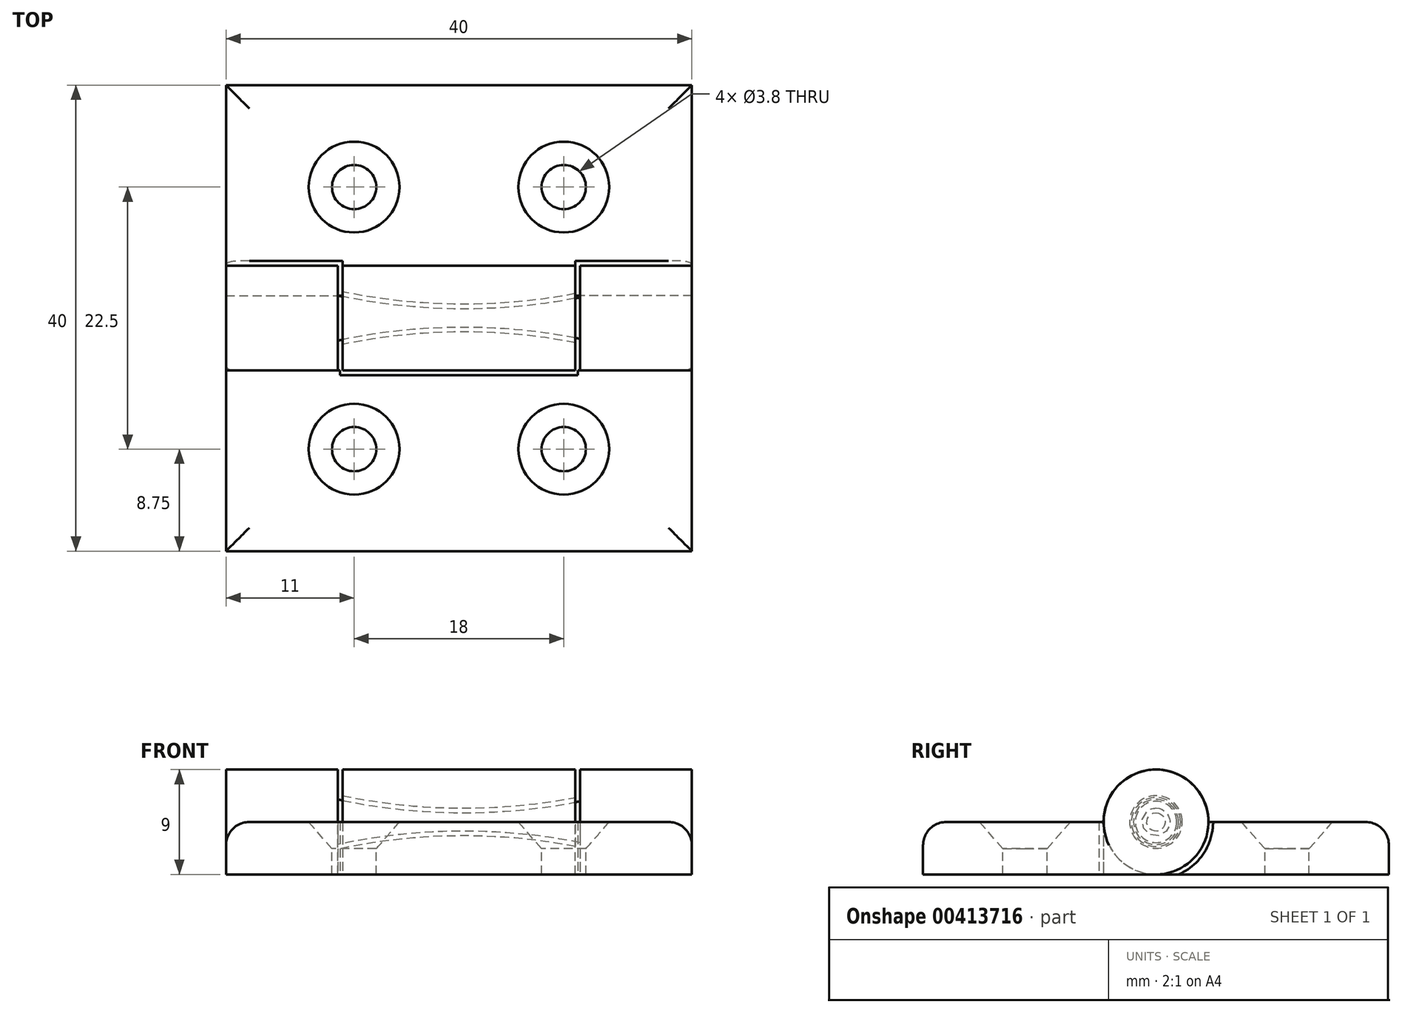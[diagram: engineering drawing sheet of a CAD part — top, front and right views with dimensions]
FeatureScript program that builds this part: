
annotation { "Feature Type Name" : "Feature", "Feature Type Description" : "" }
export const myFeature = defineFeature(function(context is Context, id is Id, definition is map)
    precondition{}
    {
        {
            var Q0;
            Q0=qCreatedBy(makeId("Front.planeOp"),FACE);
            var sketch = newSketch(context, id + "F0", { "sketchPlane" : qUnion([Q0])});
            skLineSegment(sketch, "E0", {"start": v(-18.48, 0) * mm, "end": v(18.23, 0) * mm, "construction": true});
            skLineSegment(sketch, "E1", {"start": v(-10, 18.4) * mm, "end": v(-10, -18.31) * mm, "construction": true});
            skLineSegment(sketch, "E2", {"start": v(10, 18.4) * mm, "end": v(10, -18.31) * mm, "construction": true});
            skLineSegment(sketch, "E3.0", {"start": v(-18.48, 2) * mm, "end": v(18.23, 2) * mm, "construction": true});
            skLineSegment(sketch, "E4.0", {"start": v(-18.48, 1) * mm, "end": v(18.48, 1) * mm, "construction": true});
            skPoint(sketch, "E5", {"position": v(0, 1) * mm});
            skPoint(sketch, "E6", {"position": v(10, 2) * mm});
            skPoint(sketch, "E7", {"position": v(-10, 2) * mm});
            skArc(sketch, "E8", {"start": v(-10, 2) * mm, "mid": v(0, 1) * mm, "end": v(10, 2) * mm});
            skLineSegment(sketch, "E9", {"start": v(-10, 2) * mm, "end": v(-10, 0) * mm});
            skLineSegment(sketch, "E10", {"start": v(-10, 0) * mm, "end": v(10, 0) * mm});
            skLineSegment(sketch, "E11", {"start": v(10, 0) * mm, "end": v(10, 2) * mm});
            skSolve(sketch);
        }
        {
            var Q0;
            Q0=qCreatedBy(makeId("Front.planeOp"),FACE);
            var sketch = newSketch(context, id + "F1", { "sketchPlane" : qUnion([Q0])});
            skLineSegment(sketch, "E12.0", {"start": v(-10, 0) * mm, "end": v(10, 0) * mm});
            skLineSegment(sketch, "E13.0", {"start": v(-10, 1.85) * mm, "end": v(-10, 0) * mm});
            skLineSegment(sketch, "E14.0", {"start": v(10, 0) * mm, "end": v(10, 1.7) * mm});
            skLineSegment(sketch, "E15.0", {"start": v(10.4, 0) * mm, "end": v(10.4, 2.18) * mm});
            skArc(sketch, "E15.1", {"start": v(-10.4, 2.34) * mm, "mid": v(0, 1.2) * mm, "end": v(10.4, 2.18) * mm});
            skLineSegment(sketch, "E15.2", {"start": v(-10.4, 2.34) * mm, "end": v(-10.4, 0) * mm});
            skLineSegment(sketch, "E16", {"start": v(-10.4, 0) * mm, "end": v(-10, 0) * mm});
            skLineSegment(sketch, "E17", {"start": v(-10.4, 2.34) * mm, "end": v(-10.4, 4.5) * mm});
            skLineSegment(sketch, "E18", {"start": v(-10.4, 4.5) * mm, "end": v(10.4, 4.5) * mm});
            skLineSegment(sketch, "E19", {"start": v(10.4, 4.5) * mm, "end": v(10.4, 2.18) * mm});
            skLineSegment(sketch, "E20", {"start": v(-10, 2.26) * mm, "end": v(-10, 4.5) * mm});
            skLineSegment(sketch, "E21", {"start": v(10, 2.1) * mm, "end": v(10, 4.5) * mm});
            skArc(sketch, "E22.0", {"start": v(-10.4, 1.93) * mm, "mid": v(0, 0.8) * mm, "end": v(10.4, 1.77) * mm});
            skLineSegment(sketch, "E23", {"start": v(-10, 2.26) * mm, "end": v(-10, 1.85) * mm});
            skLineSegment(sketch, "E24", {"start": v(10, 2.1) * mm, "end": v(10, 1.7) * mm});
            skLineSegment(sketch, "E25", {"start": v(10.4, 0) * mm, "end": v(10, 0) * mm});
            skSolve(sketch);
        }
        {
            var Q0;
            Q0=makeQuery(id+"F1.imprint","IMPRINT",FACE,{"disambiguationData":[TD([[makeQuery(id+"F1.imprint","IMPRINT",EDGE,{"derivedFrom":sQuery(id+"F1.wireOp",EDGE,"E12.0")}),1.0]])]});
            var Q1;
            {var subQ0=sQuery(id+"F1.wireOp",EDGE,"E13.0");Q1=makeQuery(id+"F1.imprint","IMPRINT",FACE,{"disambiguationData":[TD([[makeQuery(id+"F1.imprint","IMPRINT",EDGE,{"derivedFrom":subQ0}),-1.0]])]});}
            var Q2;
            {var subQ0=sQuery(id+"F1.wireOp",EDGE,"E14.0");Q2=makeQuery(id+"F1.imprint","IMPRINT",FACE,{"disambiguationData":[TD([[makeQuery(id+"F1.imprint","IMPRINT",EDGE,{"derivedFrom":subQ0}),-1.0]])]});}
            var Q3;
            Q3=sQuery(id+"F1.wireOp",EDGE,"E12.0");
            revolve(context, id + "F2", {"entities" : qUnion([Q0, Q1, Q2]), "axis" : qUnion([Q3]), "revolveType" : RevolveType.FULL});
        }
        {
            var Q0;
            {var subQ0=sQuery(id+"F1.wireOp",EDGE,"E20");Q0=makeQuery(id+"F1.imprint","IMPRINT",FACE,{"disambiguationData":[TD([[makeQuery(id+"F1.imprint","IMPRINT",EDGE,{"derivedFrom":subQ0}),-1.0]])]});}
            var Q1;
            Q1=sQuery(id+"F1.wireOp",EDGE,"E12.0");
            revolve(context, id + "F3", {"entities" : qUnion([Q0]), "axis" : qUnion([Q1]), "revolveType" : RevolveType.FULL});
        }
        {
            var Q0;
            Q0=qCreatedBy(makeId("Right.planeOp"),FACE);
            var sketch = newSketch(context, id + "F4", { "sketchPlane" : qUnion([Q0])});
            skPoint(sketch, "E26", {"position": v(4.5, 0) * mm});
            skLineSegment(sketch, "E27.0", {"start": v(-20, 18.4) * mm, "end": v(-20, -18.31) * mm, "construction": true});
            skLineSegment(sketch, "E28", {"start": v(-23.98, 0) * mm, "end": v(20, 0) * mm, "construction": true});
            skLineSegment(sketch, "E29.0", {"start": v(-23.98, -4.5) * mm, "end": v(20, -4.5) * mm, "construction": true});
            skPoint(sketch, "E30", {"position": v(-20, 0) * mm});
            skPoint(sketch, "E31", {"position": v(-20, -4.5) * mm});
            skPoint(sketch, "E32", {"position": v(4.5, -4.5) * mm});
            skLineSegment(sketch, "E33", {"start": v(-20, 0) * mm, "end": v(-20, -4.5) * mm});
            skLineSegment(sketch, "E34", {"start": v(4.5, -4.5) * mm, "end": v(4.5, 0) * mm});
            skLineSegment(sketch, "E35", {"start": v(-20, 0) * mm, "end": v(4.5, 0) * mm});
            skLineSegment(sketch, "E36", {"start": v(4.5, -4.5) * mm, "end": v(-20, -4.5) * mm});
            skLineSegment(sketch, "E37.0", {"start": v(20, 18.4) * mm, "end": v(20, -18.31) * mm, "construction": true});
            skPoint(sketch, "E38", {"position": v(-4.5, 0) * mm});
            skPoint(sketch, "E39", {"position": v(-20.6, 23.68) * mm});
            skLineSegment(sketch, "E40", {"start": v(-4.5, 0) * mm, "end": v(-4.5, -4.5) * mm});
            skLineSegment(sketch, "E41", {"start": v(4.5, 0) * mm, "end": v(20, 0) * mm});
            skLineSegment(sketch, "E42", {"start": v(20, -4.5) * mm, "end": v(20, 0) * mm});
            skLineSegment(sketch, "E43", {"start": v(20, -4.5) * mm, "end": v(4.5, -4.5) * mm});
            skCircle(sketch, "E44.0", {"center": v(0, 0) * mm, "radius": 4.5 * mm});
            skSolve(sketch);
        }
        {
            var Q0;
            Q0=qCreatedBy(makeId("Right.planeOp"),FACE);
            cPlane(context, id + "F5", {"entities" : qUnion([Q0]), "cplaneType" : CPlaneType.OFFSET, "offset" : 20 * mm, "width" : 150 * mm, "height" : 150 * mm});
        }
        {
            var Q0;
            Q0=qCreatedBy(makeId("Right.planeOp"),FACE);
            cPlane(context, id + "F6", {"entities" : qUnion([Q0]), "cplaneType" : CPlaneType.OFFSET, "offset" : 20 * mm, "oppositeDirection" : true, "width" : 150 * mm, "height" : 150 * mm});
        }
        {
            var Q0;
            Q0=makeQuery(id+"F4.imprint","IMPRINT",FACE,{"disambiguationData":[TD([[makeQuery(id+"F4.imprint","IMPRINT",EDGE,{"derivedFrom":sQuery(id+"F4.wireOp",EDGE,"E34")}),-1.0]])]});
            var Q1;
            {var subQ0=sQuery(id+"F4.wireOp",EDGE,"E34");Q1=makeQuery(id+"F4.imprint","IMPRINT",FACE,{"disambiguationData":[TD([[makeQuery(id+"F4.imprint","IMPRINT",EDGE,{"derivedFrom":subQ0}),1.0]])]});}
            var Q2;
            Q2=makeQuery(id+"F3.opRevolve","SWEPT_FACE",FACE,{"disambiguationData":[OSD([sQuery(id+"F1.wireOp",EDGE,"E21")])]});
            var Q3;
            Q3=makeQuery(id+"F3.opRevolve","SWEPT_FACE",FACE,{"disambiguationData":[OSD([sQuery(id+"F1.wireOp",EDGE,"E20")])]});
            extrude(context, id + "F7", {"entities" : qUnion([Q0, Q1]), "operationType" : NewBodyOperationType.ADD, "endBound" : BoundingType.UP_TO_SURFACE, "endBoundEntityFace" : qUnion([Q2]), "depth" : 25 * mm, "hasSecondDirection" : true, "secondDirectionBound" : SecondDirectionBoundingType.UP_TO_SURFACE, "secondDirectionOppositeDirection" : true, "secondDirectionBoundEntityFace" : qUnion([Q3]), "secondDirectionDepth" : 25 * mm});
        }
        {
            var Q0;
            Q0=qCreatedBy(id+"F5.planeOp",FACE);
            var sketch = newSketch(context, id + "F8", { "sketchPlane" : qUnion([Q0])});
            skLineSegment(sketch, "E45.0", {"start": v(-20, 0) * mm, "end": v(4.5, 0) * mm});
            skLineSegment(sketch, "E46.0", {"start": v(-4.5, 0) * mm, "end": v(-4.5, -4.5) * mm});
            skLineSegment(sketch, "E47.0", {"start": v(4.5, -4.5) * mm, "end": v(-20, -4.5) * mm});
            skLineSegment(sketch, "E48.0", {"start": v(-20, 0) * mm, "end": v(-20, -4.5) * mm});
            skCircle(sketch, "E49.0", {"center": v(0, 0) * mm, "radius": 4.5 * mm});
            skLineSegment(sketch, "E50.0", {"start": v(-4.9, 0) * mm, "end": v(-4.9, -4.5) * mm});
            skSolve(sketch);
        }
        {
            var Q0;
            {var subQ0=sQuery(id+"F8.wireOp",EDGE,"E49.0");var subQ1=sQuery(id+"F8.wireOp",EDGE,"E45.0");var subQ2=makeQuery(id+"F8.imprint","INTERSECT",VERTEX,{"derivedFrom":[subQ1,subQ0]});Q0=makeQuery(id+"F8.imprint","IMPRINT",FACE,{"disambiguationData":[TD([[makeQuery(id+"F8.imprint","IMPRINT",EDGE,{"disambiguationData":[TD([[subQ2,1.0]])],"derivedFrom":subQ1}),1.0]])]});}
            var Q1;
            {var subQ0=sQuery(id+"F8.wireOp",EDGE,"E49.0");var subQ1=sQuery(id+"F8.wireOp",EDGE,"E45.0");var subQ2=makeQuery(id+"F8.imprint","INTERSECT",VERTEX,{"derivedFrom":[subQ1,subQ0]});Q1=makeQuery(id+"F8.imprint","IMPRINT",FACE,{"disambiguationData":[TD([[makeQuery(id+"F8.imprint","IMPRINT",EDGE,{"disambiguationData":[TD([[subQ2,1.0]])],"derivedFrom":subQ0}),1.0]])]});}
            var Q2;
            {var subQ0=sQuery(id+"F8.wireOp",EDGE,"E46.0");Q2=makeQuery(id+"F8.imprint","IMPRINT",FACE,{"disambiguationData":[TD([[makeQuery(id+"F8.imprint","IMPRINT",EDGE,{"derivedFrom":subQ0}),1.0]])]});}
            var Q3;
            Q3=makeQuery(id+"F2.opRevolve","SWEPT_FACE",FACE,{"disambiguationData":[OSD([sQuery(id+"F1.wireOp",EDGE,"E15.0")])]});
            extrude(context, id + "F9", {"entities" : qUnion([Q0, Q1, Q2]), "operationType" : NewBodyOperationType.ADD, "endBound" : BoundingType.UP_TO_SURFACE, "oppositeDirection" : true, "endBoundEntityFace" : qUnion([Q3]), "depth" : 25 * mm});
        }
        {
            var Q0;
            Q0=qCreatedBy(id+"F6.planeOp",FACE);
            var sketch = newSketch(context, id + "F10", { "sketchPlane" : qUnion([Q0])});
            skCircle(sketch, "E51.0", {"center": v(0, 0) * mm, "radius": 4.5 * mm});
            skLineSegment(sketch, "E52.0", {"start": v(4.5, -4.5) * mm, "end": v(-20, -4.5) * mm});
            skLineSegment(sketch, "E53.0", {"start": v(-4.5, 0) * mm, "end": v(-4.5, -4.5) * mm});
            skLineSegment(sketch, "E54.0", {"start": v(-20, 0) * mm, "end": v(-20, -4.5) * mm});
            skLineSegment(sketch, "E55.0", {"start": v(-20, 0) * mm, "end": v(4.5, 0) * mm});
            skLineSegment(sketch, "E56.0", {"start": v(-4.9, 0) * mm, "end": v(-4.9, -4.5) * mm});
            skSolve(sketch);
        }
        {
            var Q0;
            {var subQ0=sQuery(id+"F10.wireOp",EDGE,"E55.0");var subQ1=sQuery(id+"F10.wireOp",EDGE,"E51.0");var subQ2=makeQuery(id+"F10.imprint","INTERSECT",VERTEX,{"derivedFrom":[subQ1,subQ0]});Q0=makeQuery(id+"F10.imprint","IMPRINT",FACE,{"disambiguationData":[TD([[makeQuery(id+"F10.imprint","IMPRINT",EDGE,{"disambiguationData":[TD([[subQ2,1.0]])],"derivedFrom":subQ1}),1.0]])]});}
            var Q1;
            {var subQ0=sQuery(id+"F10.wireOp",EDGE,"E55.0");var subQ1=sQuery(id+"F10.wireOp",EDGE,"E51.0");var subQ3=makeQuery(id+"F10.imprint","INTERSECT",VERTEX,{"derivedFrom":[subQ1,subQ0]});Q1=makeQuery(id+"F10.imprint","IMPRINT",FACE,{"disambiguationData":[TD([[makeQuery(id+"F10.imprint","IMPRINT",EDGE,{"disambiguationData":[TD([[subQ3,-1.0]])],"derivedFrom":subQ1}),1.0]])]});}
            var Q2;
            {var subQ0=sQuery(id+"F10.wireOp",EDGE,"E53.0");Q2=makeQuery(id+"F10.imprint","IMPRINT",FACE,{"disambiguationData":[TD([[makeQuery(id+"F10.imprint","IMPRINT",EDGE,{"derivedFrom":subQ0}),1.0]])]});}
            var Q3;
            Q3=makeQuery(id+"F2.opRevolve","SWEPT_FACE",FACE,{"disambiguationData":[OSD([sQuery(id+"F1.wireOp",EDGE,"E15.2")])]});
            extrude(context, id + "F11", {"entities" : qUnion([Q0, Q1, Q2]), "operationType" : NewBodyOperationType.ADD, "endBound" : BoundingType.UP_TO_SURFACE, "endBoundEntityFace" : qUnion([Q3]), "depth" : 25 * mm});
        }
        {
            var Q0;
            {var subQ0=sQuery(id+"F8.wireOp",EDGE,"E46.0");Q0=makeQuery(id+"F8.imprint","IMPRINT",FACE,{"disambiguationData":[TD([[makeQuery(id+"F8.imprint","IMPRINT",EDGE,{"derivedFrom":subQ0}),-1.0]])]});}
            var Q1;
            Q1=makeQuery(id+"F14.opExtrude","SWEPT_FACE",FACE,{"disambiguationData":[OSD([sQuery(id+"F8.wireOp",EDGE,"E50.0")])]});
            extrude(context, id + "F12", {"entities" : qUnion([Q0]), "operationType" : NewBodyOperationType.ADD, "oppositeDirection" : true, "endBoundEntityFace" : qUnion([Q1]), "depth" : (10 - .2) * mm});
        }
        {
            var Q0;
            {var subQ0=sQuery(id+"F10.wireOp",EDGE,"E53.0");Q0=makeQuery(id+"F10.imprint","IMPRINT",FACE,{"disambiguationData":[TD([[makeQuery(id+"F10.imprint","IMPRINT",EDGE,{"derivedFrom":subQ0}),-1.0]])]});}
            extrude(context, id + "F13", {"entities" : qUnion([Q0]), "operationType" : NewBodyOperationType.ADD, "depth" : (10 - .2) * mm});
        }
        {
            var Q0;
            {var subQ0=sQuery(id+"F8.wireOp",EDGE,"E48.0");Q0=makeQuery(id+"F8.imprint","IMPRINT",FACE,{"disambiguationData":[TD([[makeQuery(id+"F8.imprint","IMPRINT",EDGE,{"derivedFrom":subQ0}),1.0]])]});}
            var Q1;
            {var subQ0=sQuery(id+"F10.wireOp",EDGE,"E53.0");var subQ1=sQuery(id+"F10.wireOp",EDGE,"E52.0");Q1=makeQuery(id+"F13.boolean.opBoolean","MERGE",FACE,{"derivedFrom":[makeQuery(id+"F11.opExtrude","CAP_FACE",FACE,{"disambiguationData":[OSD([sQuery(id+"F10.wireOp",EDGE,"E51.0"),subQ1,subQ0])],"isStart":true}),makeQuery(id+"F13.opExtrude","CAP_FACE",FACE,{"disambiguationData":[OSD([subQ1,subQ0,sQuery(id+"F10.wireOp",EDGE,"E55.0"),sQuery(id+"F10.wireOp",EDGE,"E56.0")])],"isStart":true})]});}
            extrude(context, id + "F14", {"entities" : qUnion([Q0]), "operationType" : NewBodyOperationType.ADD, "endBound" : BoundingType.UP_TO_SURFACE, "oppositeDirection" : true, "endBoundEntityFace" : qUnion([Q1]), "depth" : 40 * mm});
        }
        {
            var Q0;
            Q0=makeQuery(id+"F7.boolean.opBoolean","MERGE",FACE,{"derivedFrom":[makeQuery(id+"F3.opRevolve","SWEPT_FACE",FACE,{"disambiguationData":[OSD([sQuery(id+"F1.wireOp",EDGE,"E20")])]}),makeQuery(id+"F7.opExtrude","CAP_FACE",FACE,{"disambiguationData":[OSD([sQuery(id+"F4.wireOp",EDGE,"E36"),sQuery(id+"F4.wireOp",EDGE,"E41"),sQuery(id+"F4.wireOp",EDGE,"E42"),sQuery(id+"F4.wireOp",EDGE,"E43"),sQuery(id+"F4.wireOp",EDGE,"E44.0")])],"isStart":true})]});
            var sketch = newSketch(context, id + "F15", { "sketchPlane" : qUnion([Q0])});
            skCircle(sketch, "E57.0", {"center": v(0, 0) * mm, "radius": 4.9 * mm});
            skSolve(sketch);
        }
        {
            var Q0;
            {var subQ5=makeQuery(id+"F7.opExtrude","CAP_EDGE",EDGE,{"disambiguationData":[OSD([sQuery(id+"F4.wireOp",EDGE,"E42")])],"isStart":true});Q0=makeQuery(id+"F15.imprint","IMPRINT",FACE,{"disambiguationData":[TD([[makeQuery(id+"F15.imprint","IMPRINT",EDGE,{"derivedFrom":subQ5}),1.0]])]});}
            var Q1;
            {var subQ0=sQuery(id+"F10.wireOp",EDGE,"E53.0");var subQ1=sQuery(id+"F10.wireOp",EDGE,"E52.0");Q1=makeQuery(id+"F14.boolean.opBoolean","MERGE",FACE,{"derivedFrom":[makeQuery(id+"F13.boolean.opBoolean","MERGE",FACE,{"derivedFrom":[makeQuery(id+"F11.opExtrude","CAP_FACE",FACE,{"disambiguationData":[OSD([sQuery(id+"F10.wireOp",EDGE,"E51.0"),subQ1,subQ0])],"isStart":true}),makeQuery(id+"F13.opExtrude","CAP_FACE",FACE,{"disambiguationData":[OSD([subQ1,subQ0,sQuery(id+"F10.wireOp",EDGE,"E55.0"),sQuery(id+"F10.wireOp",EDGE,"E56.0")])],"isStart":true})]}),makeQuery(id+"F14.opExtrude","CAP_FACE",FACE,{"disambiguationData":[OSD([sQuery(id+"F8.wireOp",EDGE,"E45.0"),sQuery(id+"F8.wireOp",EDGE,"E47.0"),sQuery(id+"F8.wireOp",EDGE,"E48.0"),sQuery(id+"F8.wireOp",EDGE,"E50.0")])],"isStart":false})]});}
            extrude(context, id + "F16", {"entities" : qUnion([Q0]), "operationType" : NewBodyOperationType.ADD, "endBound" : BoundingType.UP_TO_SURFACE, "endBoundEntityFace" : qUnion([Q1]), "depth" : 25 * mm});
        }
        {
            var Q0;
            Q0=makeQuery(id+"F7.boolean.opBoolean","MERGE",FACE,{"derivedFrom":[makeQuery(id+"F3.opRevolve","SWEPT_FACE",FACE,{"disambiguationData":[OSD([sQuery(id+"F1.wireOp",EDGE,"E21")])]}),makeQuery(id+"F7.opExtrude","CAP_FACE",FACE,{"disambiguationData":[OSD([sQuery(id+"F4.wireOp",EDGE,"E36"),sQuery(id+"F4.wireOp",EDGE,"E41"),sQuery(id+"F4.wireOp",EDGE,"E42"),sQuery(id+"F4.wireOp",EDGE,"E43"),sQuery(id+"F4.wireOp",EDGE,"E44.0")])],"isStart":false})]});
            var sketch = newSketch(context, id + "F17", { "sketchPlane" : qUnion([Q0])});
            skCircle(sketch, "E58.0", {"center": v(0, 0) * mm, "radius": 4.9 * mm});
            skSolve(sketch);
        }
        {
            var Q0;
            {var subQ5=makeQuery(id+"F7.opExtrude","CAP_EDGE",EDGE,{"disambiguationData":[OSD([sQuery(id+"F4.wireOp",EDGE,"E42")])],"isStart":false});Q0=makeQuery(id+"F17.imprint","IMPRINT",FACE,{"disambiguationData":[TD([[makeQuery(id+"F17.imprint","IMPRINT",EDGE,{"derivedFrom":subQ5}),-1.0]])]});}
            var Q1;
            {var subQ0=sQuery(id+"F8.wireOp",EDGE,"E50.0");var subQ1=sQuery(id+"F8.wireOp",EDGE,"E47.0");var subQ2=sQuery(id+"F8.wireOp",EDGE,"E45.0");var subQ3=sQuery(id+"F8.wireOp",EDGE,"E46.0");Q1=makeQuery(id+"F14.boolean.opBoolean","MERGE",FACE,{"derivedFrom":[makeQuery(id+"F12.boolean.opBoolean","MERGE",FACE,{"derivedFrom":[makeQuery(id+"F9.opExtrude","CAP_FACE",FACE,{"disambiguationData":[OSD([subQ3,subQ1,sQuery(id+"F8.wireOp",EDGE,"E49.0")])],"isStart":true}),makeQuery(id+"F12.opExtrude","CAP_FACE",FACE,{"disambiguationData":[OSD([subQ2,subQ3,subQ1,subQ0])],"isStart":true})]}),makeQuery(id+"F14.opExtrude","CAP_FACE",FACE,{"disambiguationData":[OSD([subQ2,subQ1,sQuery(id+"F8.wireOp",EDGE,"E48.0"),subQ0])],"isStart":true})]});}
            extrude(context, id + "F18", {"entities" : qUnion([Q0]), "operationType" : NewBodyOperationType.ADD, "endBound" : BoundingType.UP_TO_SURFACE, "endBoundEntityFace" : qUnion([Q1]), "depth" : 25 * mm});
        }
        {
            var Q0;
            Q0=makeQuery(id+"F14.opExtrude","CAP_EDGE",EDGE,{"disambiguationData":[OSD([sQuery(id+"F4.wireOp",EDGE,"E35")])],"isStart":true});
            var Q1;
            Q1=makeQuery(id+"F14.opExtrude","SWEPT_EDGE",EDGE,{"disambiguationData":[OSD([sQuery(id+"F4.wireOp",EDGE,"E33"),sQuery(id+"F4.wireOp",EDGE,"E35")])]});
            var Q2;
            Q2=makeQuery(id+"F14.opExtrude","CAP_EDGE",EDGE,{"disambiguationData":[OSD([sQuery(id+"F4.wireOp",EDGE,"E35")])],"isStart":false});
            var Q3;
            Q3=makeQuery(id+"F18.opExtrude","CAP_EDGE",EDGE,{"disambiguationData":[OSD([sQuery(id+"F4.wireOp",EDGE,"E41")])],"isStart":false});
            var Q4;
            {var subQ0=sQuery(id+"F4.wireOp",EDGE,"E42");var subQ1=sQuery(id+"F4.wireOp",EDGE,"E41");Q4=makeQuery(id+"F18.boolean.opBoolean","MERGE",EDGE,{"derivedFrom":[makeQuery(id+"F16.boolean.opBoolean","MERGE",EDGE,{"derivedFrom":[makeQuery(id+"F7.opExtrude","TWEAK_EDGE",EDGE,{"derivedFrom":[makeQuery(id+"F4.imprint","IMPRINT",EDGE,{"derivedFrom":subQ1}),makeQuery(id+"F4.imprint","IMPRINT",EDGE,{"derivedFrom":subQ0})]}),makeQuery(id+"F16.opExtrude","SWEPT_EDGE",EDGE,{"disambiguationData":[OSD([subQ1,subQ0])]})]}),makeQuery(id+"F18.opExtrude","SWEPT_EDGE",EDGE,{"disambiguationData":[OSD([subQ1,subQ0])]})]});}
            var Q5;
            Q5=makeQuery(id+"F16.opExtrude","CAP_EDGE",EDGE,{"disambiguationData":[OSD([sQuery(id+"F4.wireOp",EDGE,"E41")])],"isStart":false});
            var Q6;
            Q6=makeQuery(id+"F14.boolean.opBoolean","MERGE",EDGE,{"derivedFrom":[makeQuery(id+"F13.opExtrude","CAP_EDGE",EDGE,{"disambiguationData":[OSD([sQuery(id+"F10.wireOp",EDGE,"E55.0")])],"isStart":true}),makeQuery(id+"F14.opExtrude","CAP_EDGE",EDGE,{"disambiguationData":[OSD([sQuery(id+"F8.wireOp",EDGE,"E45.0")])],"isStart":false})]});
            var Q7;
            Q7=makeQuery(id+"F14.opExtrude","SWEPT_EDGE",EDGE,{"disambiguationData":[OSD([sQuery(id+"F8.wireOp",EDGE,"E45.0"),sQuery(id+"F8.wireOp",EDGE,"E48.0")])]});
            var Q8;
            {var subQ0=sQuery(id+"F8.wireOp",EDGE,"E45.0");Q8=makeQuery(id+"F14.boolean.opBoolean","MERGE",EDGE,{"derivedFrom":[makeQuery(id+"F12.opExtrude","CAP_EDGE",EDGE,{"disambiguationData":[OSD([subQ0])],"isStart":true}),makeQuery(id+"F14.opExtrude","CAP_EDGE",EDGE,{"disambiguationData":[OSD([subQ0])],"isStart":true})]});}
            fillet(context, id + "F19", {"entities" : qUnion([Q0, Q1, Q2, Q3, Q4, Q5, Q6, Q7, Q8]), "radius" : 2 * mm, "allowEdgeOverflow" : false});
        }
        {
            var Q0;
            {var subQ0=sQuery(id+"F8.wireOp",EDGE,"E45.0");Q0=makeQuery(id+"F14.boolean.opBoolean","MERGE",FACE,{"derivedFrom":[makeQuery(id+"F12.opExtrude","SWEPT_FACE",FACE,{"disambiguationData":[OSD([subQ0])]}),makeQuery(id+"F13.opExtrude","SWEPT_FACE",FACE,{"disambiguationData":[OSD([sQuery(id+"F10.wireOp",EDGE,"E55.0")])]}),makeQuery(id+"F14.opExtrude","SWEPT_FACE",FACE,{"disambiguationData":[OSD([subQ0])]})]});}
            var sketch = newSketch(context, id + "F20", { "sketchPlane" : qUnion([Q0])});
            skLineSegment(sketch, "E59.0", {"start": v(-18, -4.5) * mm, "end": v(-18, -18) * mm});
            skLineSegment(sketch, "E60.0", {"start": v(-18, 18) * mm, "end": v(-18, 4.9) * mm});
            skLineSegment(sketch, "E61.0", {"start": v(-20, 20) * mm, "end": v(20, 20) * mm});
            skLineSegment(sketch, "E62.0", {"start": v(10, 4.5) * mm, "end": v(-10, 4.5) * mm});
            skLineSegment(sketch, "E63.0", {"start": v(-10.2, -4.9) * mm, "end": v(10.2, -4.9) * mm});
            skLineSegment(sketch, "E64.0", {"start": v(18, 18) * mm, "end": v(-18, 18) * mm});
            skLineSegment(sketch, "E65", {"start": v(9, 4.5) * mm, "end": v(9, 18) * mm, "construction": true});
            skPoint(sketch, "E66.startSnap0", {"position": v(0, 18) * mm});
            skLineSegment(sketch, "E67.0", {"start": v(18, 4.9) * mm, "end": v(18, 18) * mm});
            skLineSegment(sketch, "E68", {"start": v(0, 11.25) * mm, "end": v(18, 11.25) * mm, "construction": true});
            skPoint(sketch, "E68.startSnap0", {"position": v(9, 11.25) * mm});
            skPoint(sketch, "E69.MirrorP", {"position": v(-9, 11.25) * mm});
            skPoint(sketch, "E70.MirrorP", {"position": v(-9, -11.25) * mm});
            skPoint(sketch, "E71.MirrorP", {"position": v(9, -11.25) * mm});
            skSolve(sketch);
        }
        {
            var Q0;
            Q0=sQuery(id+"F20.wireOp",VERTEX,"E68.startSnap0");
            var Q1;
            Q1=sQuery(id+"F20.wireOp",VERTEX,"E69.MirrorP");
            var Q2;
            Q2=sQuery(id+"F20.wireOp",VERTEX,"E70.MirrorP");
            var Q3;
            Q3=sQuery(id+"F20.wireOp",VERTEX,"E71.MirrorP");
            var Q4;
            Q4=makeQuery(id+"F2.opRevolve","SWEPT_BODY",BODY,{"disambiguationData":[OSD([sQuery(id+"F1.wireOp",EDGE,"E12.0"),sQuery(id+"F1.wireOp",EDGE,"E15.0"),sQuery(id+"F1.wireOp",EDGE,"E15.2"),sQuery(id+"F1.wireOp",EDGE,"E16"),sQuery(id+"F1.wireOp",EDGE,"E22.0"),sQuery(id+"F1.wireOp",EDGE,"E25")])]});
            var Q5;
            Q5=makeQuery(id+"F3.opRevolve","SWEPT_BODY",BODY,{"disambiguationData":[OSD([sQuery(id+"F1.wireOp",EDGE,"E15.1"),sQuery(id+"F1.wireOp",EDGE,"E18"),sQuery(id+"F1.wireOp",EDGE,"E20"),sQuery(id+"F1.wireOp",EDGE,"E21")])]});
            hole(context, id + "F21", {"style" : HoleStyle.C_SINK, "endStyle" : HoleEndStyle.THROUGH, "standardTappedOrClearance" : lookupTablePath({ "standard" : "ANSI", "fit" : "Normal (ASME)", "size" : "#6", "type" : "Clearance" }), "standardBlindInLast" : lookupTablePath({ "fit" : "Free", "standard" : "ANSI", "size" : "#6", "type" : "Clearance" }), "holeDiameter" : 3.8 * mm, "cSinkDiameter" : 7.8 * mm, "cSinkAngle" : 82 * degree, "isTappedThrough" : true, "tappedDepth" : 12 * mm, "tapClearance" : 3, "locations" : qUnion([Q0, Q1, Q2, Q3]), "scope" : qUnion([Q4, Q5])});
        }
    });
